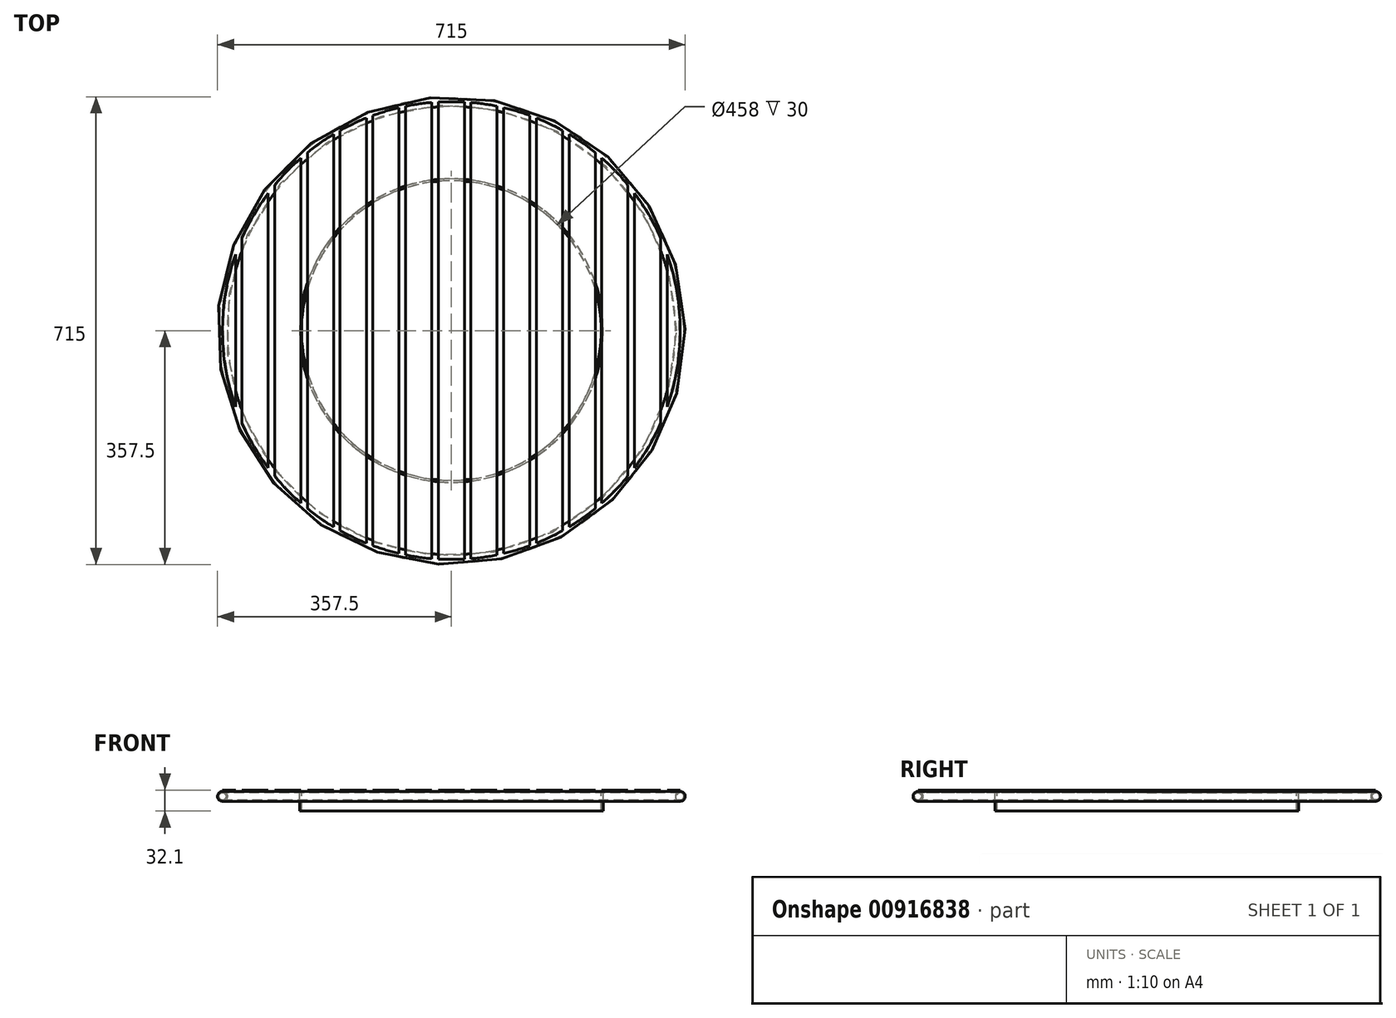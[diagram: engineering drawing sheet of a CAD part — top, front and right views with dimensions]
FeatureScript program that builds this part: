
annotation { "Feature Type Name" : "Feature", "Feature Type Description" : "" }
export const myFeature = defineFeature(function(context is Context, id is Id, definition is map)
    precondition{}
    {
        {
            var Q0;
            Q0=qCreatedBy(makeId("Top.planeOp"),FACE);
            var sketch = newSketch(context, id + "F0", { "sketchPlane" : qUnion([Q0])});
            skCircle(sketch, "E0", {"center": v(0, 0) * mm, "radius": 350 * mm});
            skSolve(sketch);
        }
        {
            var Q0;
            Q0=qCreatedBy(makeId("Front.planeOp"),FACE);
            var sketch = newSketch(context, id + "F1", { "sketchPlane" : qUnion([Q0])});
            skCircle(sketch, "E1", {"center": v(-350, 0) * mm, "radius": 7.5 * mm});
            skCircle(sketch, "E2", {"center": v(-350, 0) * mm, "radius": 5.5 * mm});
            skSolve(sketch);
        }
        {
            var Q0;
            Q0=makeQuery(id+"F1.imprint","IMPRINT",FACE,{"disambiguationData":[TD([[makeQuery(id+"F1.imprint","IMPRINT",EDGE,{"derivedFrom":sQuery(id+"F1.wireOp",EDGE,"E1")}),1.0]])]});
            var Q1;
            Q1=sQuery(id+"F0.wireOp",EDGE,"E0");
            sweep(context, id + "F2", {"profiles" : qUnion([Q0]), "path" : qUnion([Q1])});
        }
        {
            var Q0;
            Q0=qCreatedBy(makeId("Top.planeOp"),FACE);
            cPlane(context, id + "F3", {"entities" : qUnion([Q0]), "cplaneType" : CPlaneType.OFFSET, "offset" : 7.5 * mm, "width" : 150 * mm, "height" : 150 * mm});
        }
        {
            var Q0;
            Q0=qCreatedBy(id+"F3.planeOp",FACE);
            var sketch = newSketch(context, id + "F4", { "sketchPlane" : qUnion([Q0])});
            skCircle(sketch, "E3", {"center": v(0, 0) * mm, "radius": 350 * mm});
            skLineSegment(sketch, "E4.bottom", {"start": v(-20, 349.43) * mm, "end": v(20, 349.43) * mm});
            skLineSegment(sketch, "E4.top", {"start": v(-20, -349.43) * mm, "end": v(20, -349.43) * mm});
            skLineSegment(sketch, "E4.left", {"start": v(-20, 349.43) * mm, "end": v(-20, -349.43) * mm});
            skLineSegment(sketch, "E4.right", {"start": v(20, 349.43) * mm, "end": v(20, -349.43) * mm});
            skLineSegment(sketch, "E5.left", {"start": v(-30, 348.71) * mm, "end": v(-30, -348.71) * mm});
            skLineSegment(sketch, "E5.right", {"start": v(-70, 342.93) * mm, "end": v(-70, -342.93) * mm});
            skPoint(sketch, "E5.middle", {"position": v(-50, 0) * mm});
            skLineSegment(sketch, "E6.left", {"start": v(-80, 340.73) * mm, "end": v(-80, -340.73) * mm});
            skLineSegment(sketch, "E6.right", {"start": v(-120, 328.79) * mm, "end": v(-120, -328.79) * mm});
            skPoint(sketch, "E6.middle", {"position": v(-100, 0) * mm});
            skLineSegment(sketch, "E7.left", {"start": v(-130, 324.96) * mm, "end": v(-130, -324.96) * mm});
            skLineSegment(sketch, "E7.right", {"start": v(-170, 305.94) * mm, "end": v(-170, -305.94) * mm});
            skPoint(sketch, "E7.middle", {"position": v(-150, 0) * mm});
            skLineSegment(sketch, "E8.left", {"start": v(-180, 300.17) * mm, "end": v(-180, -300.17) * mm});
            skLineSegment(sketch, "E8.right", {"start": v(-220, 272.21) * mm, "end": v(-220, -272.21) * mm});
            skPoint(sketch, "E8.middle", {"position": v(-200, 0) * mm});
            skLineSegment(sketch, "E9.left", {"start": v(-230, 263.82) * mm, "end": v(-230, -263.82) * mm});
            skLineSegment(sketch, "E9.right", {"start": v(-270, 222.71) * mm, "end": v(-270, -222.71) * mm});
            skPoint(sketch, "E9.middle", {"position": v(-250, 0) * mm});
            skLineSegment(sketch, "E10", {"start": v(-280, -210) * mm, "end": v(-280, 210) * mm});
            skPoint(sketch, "E11.orphan", {"position": v(-270, 263.82) * mm});
            skPoint(sketch, "E12.orphan", {"position": v(-220, 300.17) * mm});
            skPoint(sketch, "E13.orphan", {"position": v(-170, 324.96) * mm});
            skPoint(sketch, "E14.orphan", {"position": v(-120, 340.73) * mm});
            skPoint(sketch, "E15.orphan", {"position": v(-70, 348.71) * mm});
            skPoint(sketch, "E5.top.end.orphan", {"position": v(-70, -348.71) * mm});
            skPoint(sketch, "E16.orphan", {"position": v(-120, -340.73) * mm});
            skPoint(sketch, "E17.orphan", {"position": v(-170, -324.96) * mm});
            skPoint(sketch, "E18.orphan", {"position": v(-220, -300.17) * mm});
            skPoint(sketch, "E9.top.end.orphan", {"position": v(-270, -263.82) * mm});
            skLineSegment(sketch, "E19", {"start": v(-320, 141.77) * mm, "end": v(-320, -141.77) * mm});
            skLineSegment(sketch, "E20", {"start": v(0, 0) * mm, "end": v(0, 56.7) * mm});
            skLineSegment(sketch, "E21.MirrorCS", {"start": v(30, 348.71) * mm, "end": v(30, -348.71) * mm});
            skLineSegment(sketch, "E22.MirrorCS", {"start": v(70, 342.93) * mm, "end": v(70, -342.93) * mm});
            skLineSegment(sketch, "E23.MirrorCS", {"start": v(80, 340.73) * mm, "end": v(80, -340.73) * mm});
            skLineSegment(sketch, "E24.MirrorCS", {"start": v(120, 328.79) * mm, "end": v(120, -328.79) * mm});
            skLineSegment(sketch, "E25.MirrorCS", {"start": v(130, 324.96) * mm, "end": v(130, -324.96) * mm});
            skLineSegment(sketch, "E26.MirrorCS", {"start": v(170, 305.94) * mm, "end": v(170, -305.94) * mm});
            skLineSegment(sketch, "E27.MirrorCS", {"start": v(180, 300.17) * mm, "end": v(180, -300.17) * mm});
            skLineSegment(sketch, "E28.MirrorCS", {"start": v(220, 272.21) * mm, "end": v(220, -272.21) * mm});
            skLineSegment(sketch, "E29.MirrorCS", {"start": v(230, 263.82) * mm, "end": v(230, -263.82) * mm});
            skLineSegment(sketch, "E30.MirrorCS", {"start": v(270, 222.71) * mm, "end": v(270, -222.71) * mm});
            skLineSegment(sketch, "E31.MirrorCS", {"start": v(320, 141.77) * mm, "end": v(320, -141.77) * mm});
            skLineSegment(sketch, "E32", {"start": v(-330, -116.62) * mm, "end": v(-330, 116.62) * mm});
            skLineSegment(sketch, "E33.MirrorCS", {"start": v(330, -116.62) * mm, "end": v(330, 116.62) * mm});
            skLineSegment(sketch, "E34.MirrorCS", {"start": v(280, -210) * mm, "end": v(280, 210) * mm});
            skSolve(sketch);
        }
        {
            var Q0;
            {var subQ0=sQuery(id+"F4.wireOp",EDGE,"E10");Q0=makeQuery(id+"F4.imprint","IMPRINT",FACE,{"disambiguationData":[TD([[makeQuery(id+"F4.imprint","IMPRINT",EDGE,{"derivedFrom":subQ0}),1.0]])]});}
            var Q1;
            {var subQ0=sQuery(id+"F4.wireOp",EDGE,"E9.left");Q1=makeQuery(id+"F4.imprint","IMPRINT",FACE,{"disambiguationData":[TD([[makeQuery(id+"F4.imprint","IMPRINT",EDGE,{"derivedFrom":subQ0}),-1.0]])]});}
            var Q2;
            {var subQ0=sQuery(id+"F4.wireOp",EDGE,"E8.left");Q2=makeQuery(id+"F4.imprint","IMPRINT",FACE,{"disambiguationData":[TD([[makeQuery(id+"F4.imprint","IMPRINT",EDGE,{"derivedFrom":subQ0}),-1.0]])]});}
            var Q3;
            {var subQ0=sQuery(id+"F4.wireOp",EDGE,"E7.left");Q3=makeQuery(id+"F4.imprint","IMPRINT",FACE,{"disambiguationData":[TD([[makeQuery(id+"F4.imprint","IMPRINT",EDGE,{"derivedFrom":subQ0}),-1.0]])]});}
            var Q4;
            {var subQ0=sQuery(id+"F4.wireOp",EDGE,"E6.left");Q4=makeQuery(id+"F4.imprint","IMPRINT",FACE,{"disambiguationData":[TD([[makeQuery(id+"F4.imprint","IMPRINT",EDGE,{"derivedFrom":subQ0}),-1.0]])]});}
            var Q5;
            {var subQ0=sQuery(id+"F4.wireOp",EDGE,"E5.left");Q5=makeQuery(id+"F4.imprint","IMPRINT",FACE,{"disambiguationData":[TD([[makeQuery(id+"F4.imprint","IMPRINT",EDGE,{"derivedFrom":subQ0}),-1.0]])]});}
            var Q6;
            Q6=makeQuery(id+"F4.imprint","IMPRINT",FACE,{"disambiguationData":[TD([[makeQuery(id+"F4.imprint","IMPRINT",EDGE,{"derivedFrom":sQuery(id+"F4.wireOp",EDGE,"E4.bottom")}),-1.0]])]});
            var Q7;
            {var subQ0=sQuery(id+"F4.wireOp",EDGE,"bfba225b-0817-4681-92a3-a46d2f063d4f0.MirrorCS");Q7=makeQuery(id+"F4.imprint","IMPRINT",FACE,{"disambiguationData":[TD([[makeQuery(id+"F4.imprint","IMPRINT",EDGE,{"derivedFrom":subQ0}),1.0]])]});}
            var Q8;
            {var subQ0=sQuery(id+"F4.wireOp",EDGE,"4912d06f-867c-44fb-9bcd-f5812b19cd6d0.MirrorCS");Q8=makeQuery(id+"F4.imprint","IMPRINT",FACE,{"disambiguationData":[TD([[makeQuery(id+"F4.imprint","IMPRINT",EDGE,{"derivedFrom":subQ0}),1.0]])]});}
            var Q9;
            {var subQ0=sQuery(id+"F4.wireOp",EDGE,"925a19c4-8f17-457f-9d0c-9387584e392c0.MirrorCS");Q9=makeQuery(id+"F4.imprint","IMPRINT",FACE,{"disambiguationData":[TD([[makeQuery(id+"F4.imprint","IMPRINT",EDGE,{"derivedFrom":subQ0}),1.0]])]});}
            var Q10;
            {var subQ0=sQuery(id+"F4.wireOp",EDGE,"22827606-f565-4dab-a49a-1f7b6423c8670.MirrorCS");Q10=makeQuery(id+"F4.imprint","IMPRINT",FACE,{"disambiguationData":[TD([[makeQuery(id+"F4.imprint","IMPRINT",EDGE,{"derivedFrom":subQ0}),1.0]])]});}
            var Q11;
            {var subQ0=sQuery(id+"F4.wireOp",EDGE,"55085a65-a3d1-4f32-8ddb-19d53a40a6160.MirrorCS");Q11=makeQuery(id+"F4.imprint","IMPRINT",FACE,{"disambiguationData":[TD([[makeQuery(id+"F4.imprint","IMPRINT",EDGE,{"derivedFrom":subQ0}),1.0]])]});}
            var Q12;
            {var subQ0=sQuery(id+"F4.wireOp",EDGE,"f9055472-6f82-4a08-91fa-8c525d6d7d5f0.MirrorCS");Q12=makeQuery(id+"F4.imprint","IMPRINT",FACE,{"disambiguationData":[TD([[makeQuery(id+"F4.imprint","IMPRINT",EDGE,{"derivedFrom":subQ0}),-1.0]])]});}
            var Q13;
            {var subQ0=sQuery(id+"F4.wireOp",EDGE,"E32");Q13=makeQuery(id+"F4.imprint","IMPRINT",FACE,{"disambiguationData":[TD([[makeQuery(id+"F4.imprint","IMPRINT",EDGE,{"derivedFrom":subQ0}),1.0]])]});}
            var Q14;
            {var subQ0=sQuery(id+"F4.wireOp",EDGE,"E21.MirrorCS");Q14=makeQuery(id+"F4.imprint","IMPRINT",FACE,{"disambiguationData":[TD([[makeQuery(id+"F4.imprint","IMPRINT",EDGE,{"derivedFrom":subQ0}),1.0]])]});}
            var Q15;
            {var subQ0=sQuery(id+"F4.wireOp",EDGE,"E23.MirrorCS");Q15=makeQuery(id+"F4.imprint","IMPRINT",FACE,{"disambiguationData":[TD([[makeQuery(id+"F4.imprint","IMPRINT",EDGE,{"derivedFrom":subQ0}),1.0]])]});}
            var Q16;
            {var subQ0=sQuery(id+"F4.wireOp",EDGE,"E25.MirrorCS");Q16=makeQuery(id+"F4.imprint","IMPRINT",FACE,{"disambiguationData":[TD([[makeQuery(id+"F4.imprint","IMPRINT",EDGE,{"derivedFrom":subQ0}),1.0]])]});}
            var Q17;
            {var subQ0=sQuery(id+"F4.wireOp",EDGE,"E27.MirrorCS");Q17=makeQuery(id+"F4.imprint","IMPRINT",FACE,{"disambiguationData":[TD([[makeQuery(id+"F4.imprint","IMPRINT",EDGE,{"derivedFrom":subQ0}),1.0]])]});}
            var Q18;
            {var subQ0=sQuery(id+"F4.wireOp",EDGE,"E29.MirrorCS");Q18=makeQuery(id+"F4.imprint","IMPRINT",FACE,{"disambiguationData":[TD([[makeQuery(id+"F4.imprint","IMPRINT",EDGE,{"derivedFrom":subQ0}),1.0]])]});}
            var Q19;
            {var subQ0=sQuery(id+"F4.wireOp",EDGE,"E33.MirrorCS");Q19=makeQuery(id+"F4.imprint","IMPRINT",FACE,{"disambiguationData":[TD([[makeQuery(id+"F4.imprint","IMPRINT",EDGE,{"derivedFrom":subQ0}),-1.0]])]});}
            var Q20;
            {var subQ0=sQuery(id+"F4.wireOp",EDGE,"E31.MirrorCS");Q20=makeQuery(id+"F4.imprint","IMPRINT",FACE,{"disambiguationData":[TD([[makeQuery(id+"F4.imprint","IMPRINT",EDGE,{"derivedFrom":subQ0}),-1.0]])]});}
            extrude(context, id + "F5", {"entities" : qUnion([Q0, Q1, Q2, Q3, Q4, Q5, Q6, Q7, Q8, Q9, Q10, Q11, Q12, Q13, Q14, Q15, Q16, Q17, Q18, Q19, Q20]), "operationType" : NewBodyOperationType.ADD, "depth" : 2 * mm, "offsetDistance" : 25 * mm, "hasSecondDirection" : true, "secondDirectionOppositeDirection" : true, "secondDirectionDepth" : .1 * mm});
        }
        {
            var Q0;
            Q0=makeQuery(id+"F5.opExtrude","CAP_FACE",FACE,{"disambiguationData":[OSD([sQuery(id+"F4.wireOp",EDGE,"E3"),sQuery(id+"F4.wireOp",EDGE,"E5.left"),sQuery(id+"F4.wireOp",EDGE,"E5.right")])],"isStart":true});
            var sketch = newSketch(context, id + "F6", { "sketchPlane" : qUnion([Q0])});
            skCircle(sketch, "E35", {"center": v(0, 0) * mm, "radius": 229 * mm});
            skCircle(sketch, "E36", {"center": v(0, 0) * mm, "radius": 232 * mm});
            skSolve(sketch);
        }
        {
            var Q0;
            Q0=qSketchRegion(id+"F6",true);
            extrude(context, id + "F7", {"entities" : qUnion([Q0]), "operationType" : NewBodyOperationType.ADD, "depth" : 30 * mm, "offsetDistance" : 25 * mm});
        }
    });
